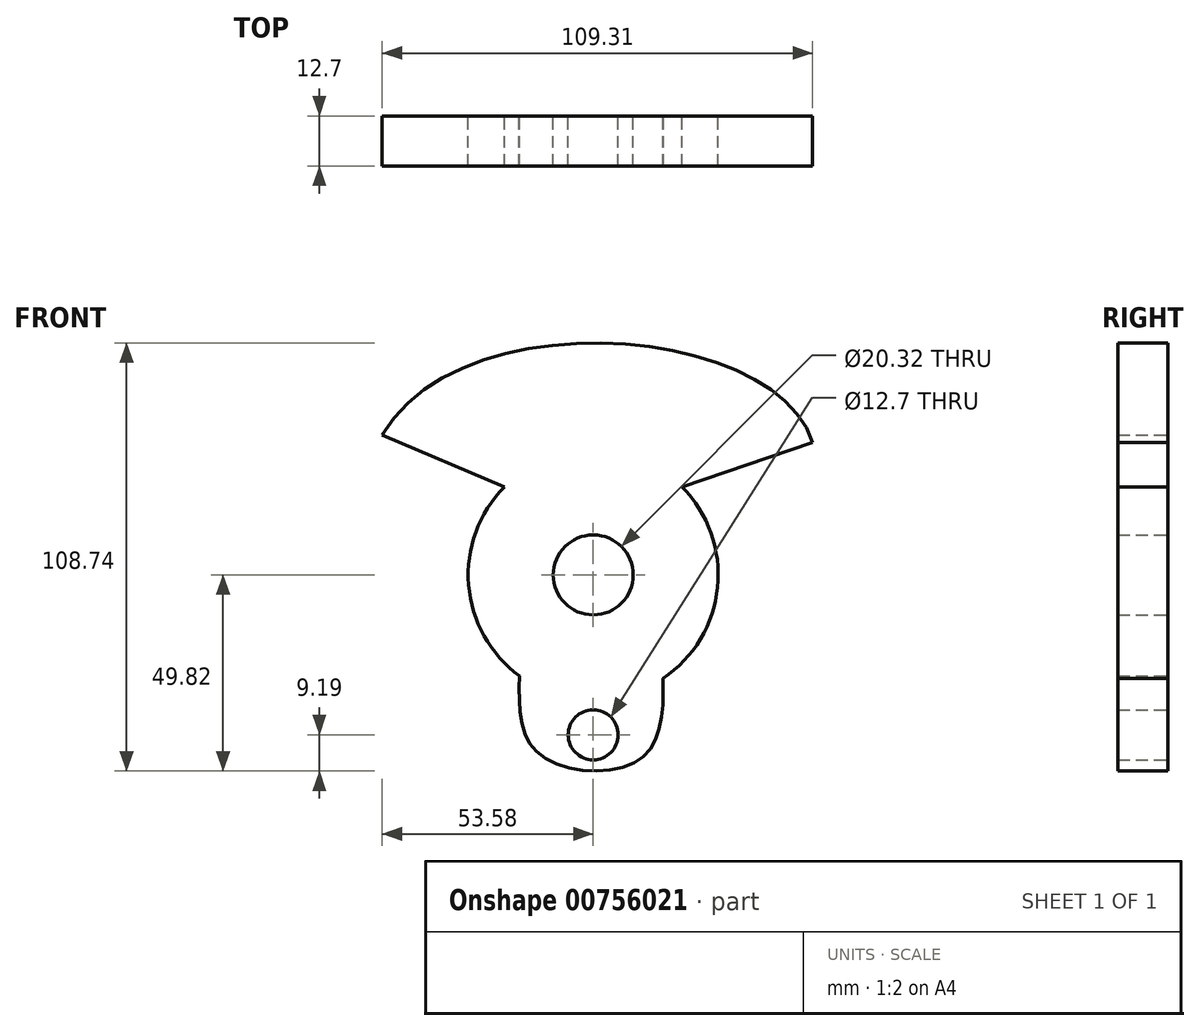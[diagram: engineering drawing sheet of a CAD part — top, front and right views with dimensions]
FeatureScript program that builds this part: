
annotation { "Feature Type Name" : "Feature", "Feature Type Description" : "" }
export const myFeature = defineFeature(function(context is Context, id is Id, definition is map)
    precondition{}
    {
        {
            var Q0;
            Q0=qCreatedBy(makeId("Front.planeOp"),FACE);
            var sketch = newSketch(context, id + "F0", { "sketchPlane" : qUnion([Q0])});
            skCircle(sketch, "E0", {"center": v(0, 0) * mm, "radius": 31.75 * mm});
            skFitSpline(sketch, "E1", {"points": [v(-18.71, -25.65) * mm, v(-13.76, -45.5) * mm, v(11.48, -47.1) * mm, v(17.75, -26.32) * mm], "startDerivative": vector(-2.08, -71.3) * mm, "endDerivative": vector(-1.98, 77.73) * mm});
            skCircle(sketch, "E2", {"center": v(0, -40.63) * mm, "radius": 6.35 * mm});
            skLineSegment(sketch, "E3", {"start": v(-22.58, 22.32) * mm, "end": v(-53.58, 35.56) * mm});
            skLineSegment(sketch, "E4", {"start": v(22.58, 22.32) * mm, "end": v(55.73, 33.7) * mm});
            skFitSpline(sketch, "E5", {"points": [v(-53.58, 35.56) * mm, v(55.73, 33.7) * mm], "startDerivative": vector(60.14, 103.92) * mm, "endDerivative": vector(28, -89.57) * mm});
            skCircle(sketch, "E6", {"center": v(0, 0) * mm, "radius": 10.16 * mm});
            skSolve(sketch);
        }
        {
            var Q0;
            {var subQ0=sQuery(id+"F0.wireOp",EDGE,"E3");Q0=makeQuery(id+"F0.imprint","IMPRINT",FACE,{"disambiguationData":[TD([[makeQuery(id+"F0.imprint","IMPRINT",EDGE,{"derivedFrom":subQ0}),-1.0]])]});}
            var Q1;
            Q1=makeQuery(id+"F0.imprint","IMPRINT",FACE,{"disambiguationData":[TD([[makeQuery(id+"F0.imprint","IMPRINT",EDGE,{"derivedFrom":sQuery(id+"F0.wireOp",EDGE,"E6")}),-1.0]])]});
            var Q2;
            {var subQ0=sQuery(id+"F0.wireOp",EDGE,"E1");Q2=makeQuery(id+"F0.imprint","IMPRINT",FACE,{"disambiguationData":[TD([[makeQuery(id+"F0.imprint","IMPRINT",EDGE,{"derivedFrom":subQ0}),1.0]])]});}
            extrude(context, id + "F1", {"entities" : qUnion([Q0, Q1, Q2]), "depth" : 12.7 * mm, "offsetDistance" : 25.4 * mm});
        }
    });
